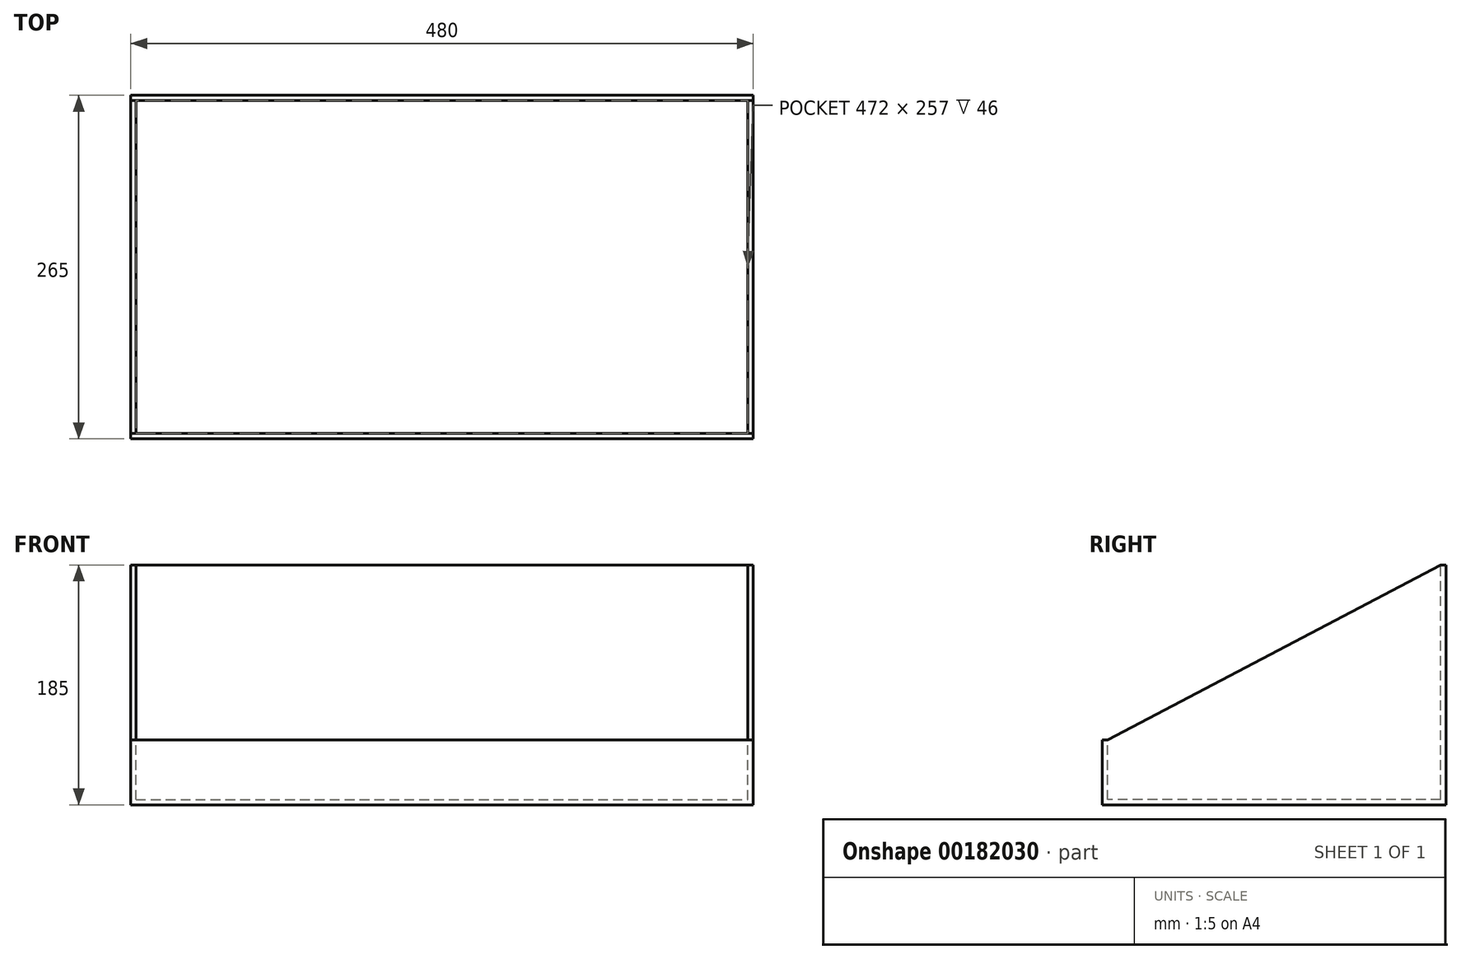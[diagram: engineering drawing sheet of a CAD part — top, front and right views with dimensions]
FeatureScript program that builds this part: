
annotation { "Feature Type Name" : "Feature", "Feature Type Description" : "" }
export const myFeature = defineFeature(function(context is Context, id is Id, definition is map)
    precondition{}
    {
        {
            var Q0;
            Q0=qCreatedBy(makeId("Front.planeOp"),FACE);
            var sketch = newSketch(context, id + "F0", { "sketchPlane" : qUnion([Q0])});
            skLineSegment(sketch, "E0.bottom", {"start": v(0, 0) * mm, "end": v(-480, 0) * mm});
            skLineSegment(sketch, "E0.top", {"start": v(0, 185) * mm, "end": v(-480, 185) * mm});
            skLineSegment(sketch, "E0.left", {"start": v(0, 0) * mm, "end": v(0, 185) * mm});
            skLineSegment(sketch, "E0.right", {"start": v(-480, 0) * mm, "end": v(-480, 185) * mm});
            skSolve(sketch);
        }
        {
            var Q0;
            Q0=qSketchRegion(id+"F0",true);
            extrude(context, id + "F1", {"entities" : qUnion([Q0]), "oppositeDirection" : true, "depth" : 265 * mm});
        }
        {
            var Q0;
            Q0=qCreatedBy(makeId("Right.planeOp"),FACE);
            var sketch = newSketch(context, id + "F2", { "sketchPlane" : qUnion([Q0])});
            skLineSegment(sketch, "E1.0", {"start": v(265, 185) * mm, "end": v(0, 185) * mm, "construction": true});
            skLineSegment(sketch, "E2", {"start": v(4, 50) * mm, "end": v(261, 185) * mm});
            skLineSegment(sketch, "E3", {"start": v(261, 185) * mm, "end": v(0, 185) * mm});
            skLineSegment(sketch, "E4", {"start": v(0, 50) * mm, "end": v(4, 50) * mm});
            skLineSegment(sketch, "E5", {"start": v(0, 185) * mm, "end": v(0, 50) * mm});
            skSolve(sketch);
        }
        {
            var Q0;
            Q0=qSketchRegion(id+"F2",true);
            extrude(context, id + "F3", {"entities" : qUnion([Q0]), "operationType" : NewBodyOperationType.REMOVE, "endBound" : BoundingType.UP_TO_NEXT, "oppositeDirection" : true, "depth" : 25 * mm});
        }
        {
            var Q0;
            Q0=qCreatedBy(makeId("Top.planeOp"),FACE);
            var Q1;
            Q1=makeQuery(id+"F3.boolean.opBoolean","COPY",VERTEX,{"derivedFrom":makeQuery(id+"F3.opExtrude","CAP_VERTEX",VERTEX,{"disambiguationData":[OSD([sQuery(id+"F2.wireOp",EDGE,"E2"),sQuery(id+"F2.wireOp",EDGE,"E3")])],"isStart":true})});
            cPlane(context, id + "F4", {"entities" : qUnion([Q0, Q1]), "cplaneType" : CPlaneType.PLANE_POINT, "offset" : 25 * mm, "width" : 150 * mm, "height" : 150 * mm});
        }
        {
            var Q0;
            Q0=qCreatedBy(id+"F4.planeOp",FACE);
            var sketch = newSketch(context, id + "F5", { "sketchPlane" : qUnion([Q0])});
            skLineSegment(sketch, "E6.0", {"start": v(0, 4) * mm, "end": v(0, 261) * mm, "construction": true});
            skLineSegment(sketch, "E6.1", {"start": v(-480, 261) * mm, "end": v(-480, 4) * mm, "construction": true});
            skLineSegment(sketch, "E7.0", {"start": v(-476, 261) * mm, "end": v(-476, 4) * mm, "construction": true});
            skLineSegment(sketch, "E8.0", {"start": v(-4, 4) * mm, "end": v(-4, 366) * mm, "construction": true});
            skLineSegment(sketch, "E9.bottom", {"start": v(-476, 261) * mm, "end": v(-4, 261) * mm});
            skLineSegment(sketch, "E9.top", {"start": v(-476, 4) * mm, "end": v(-4, 4) * mm});
            skLineSegment(sketch, "E9.left", {"start": v(-476, 261) * mm, "end": v(-476, 4) * mm});
            skLineSegment(sketch, "E9.right", {"start": v(-4, 261) * mm, "end": v(-4, 4) * mm});
            skSolve(sketch);
        }
        {
            var Q0;
            Q0=qSketchRegion(id+"F5",true);
            extrude(context, id + "F6", {"entities" : qUnion([Q0]), "operationType" : NewBodyOperationType.REMOVE, "oppositeDirection" : true, "depth" : 181 * mm});
        }
    });
